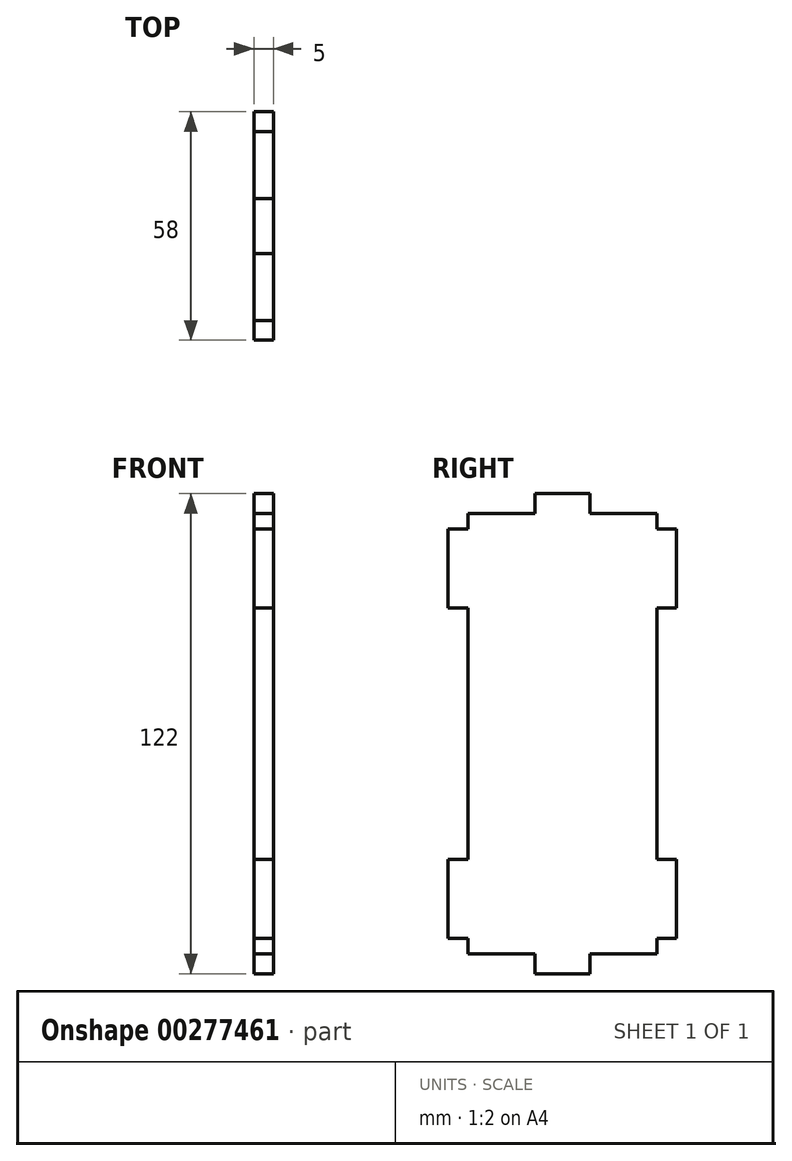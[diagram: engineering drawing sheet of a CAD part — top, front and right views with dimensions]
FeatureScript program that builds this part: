
annotation { "Feature Type Name" : "Feature", "Feature Type Description" : "" }
export const myFeature = defineFeature(function(context is Context, id is Id, definition is map)
    precondition{}
    {
        {
            var Q0;
            Q0=qCreatedBy(makeId("Right.planeOp"),FACE);
            var sketch = newSketch(context, id + "F0", { "sketchPlane" : qUnion([Q0])});
            skLineSegment(sketch, "E0.bottom", {"start": v(-24, 56) * mm, "end": v(-7, 56) * mm});
            skLineSegment(sketch, "E0.top", {"start": v(-24, -56) * mm, "end": v(-7, -56) * mm});
            skLineSegment(sketch, "E0.left", {"start": v(-24, 56) * mm, "end": v(-24, 52) * mm});
            skLineSegment(sketch, "E0.right", {"start": v(24, 56) * mm, "end": v(24, 52) * mm});
            skLineSegment(sketch, "E1.bottom", {"start": v(-24, 52) * mm, "end": v(-29, 52) * mm});
            skLineSegment(sketch, "E1.top", {"start": v(-24, 32) * mm, "end": v(-29, 32) * mm});
            skLineSegment(sketch, "E1.right", {"start": v(-29, 52) * mm, "end": v(-29, 32) * mm});
            skLineSegment(sketch, "E2.bottom", {"start": v(-24, -32) * mm, "end": v(-29, -32) * mm});
            skLineSegment(sketch, "E2.top", {"start": v(-24, -52) * mm, "end": v(-29, -52) * mm});
            skLineSegment(sketch, "E2.right", {"start": v(-29, -32) * mm, "end": v(-29, -52) * mm});
            skLineSegment(sketch, "E3.top", {"start": v(-7, 61) * mm, "end": v(7, 61) * mm});
            skLineSegment(sketch, "E3.left", {"start": v(-7, 56) * mm, "end": v(-7, 61) * mm});
            skLineSegment(sketch, "E3.right", {"start": v(7, 56) * mm, "end": v(7, 61) * mm});
            skLineSegment(sketch, "E4.top", {"start": v(-7, -61) * mm, "end": v(7, -61) * mm});
            skLineSegment(sketch, "E4.left", {"start": v(-7, -56) * mm, "end": v(-7, -61) * mm});
            skLineSegment(sketch, "E4.right", {"start": v(7, -56) * mm, "end": v(7, -61) * mm});
            skLineSegment(sketch, "E5.bottom", {"start": v(24, 52) * mm, "end": v(29, 52) * mm});
            skLineSegment(sketch, "E5.top", {"start": v(24, 32) * mm, "end": v(29, 32) * mm});
            skLineSegment(sketch, "E5.right", {"start": v(29, 52) * mm, "end": v(29, 32) * mm});
            skLineSegment(sketch, "E6.bottom", {"start": v(24, -32) * mm, "end": v(29, -32) * mm});
            skLineSegment(sketch, "E6.top", {"start": v(24, -52) * mm, "end": v(29, -52) * mm});
            skLineSegment(sketch, "E6.right", {"start": v(29, -32) * mm, "end": v(29, -52) * mm});
            skLineSegment(sketch, "E7.trimOffspring", {"start": v(7, 56) * mm, "end": v(24, 56) * mm});
            skLineSegment(sketch, "E8.trimOffspring", {"start": v(-24, -52) * mm, "end": v(-24, -56) * mm});
            skLineSegment(sketch, "E9.trimOffspring", {"start": v(24, 32) * mm, "end": v(24, -32) * mm});
            skLineSegment(sketch, "E10.trimOffspring", {"start": v(24, -52) * mm, "end": v(24, -56) * mm});
            skLineSegment(sketch, "E11.trimOffspring", {"start": v(7, -56) * mm, "end": v(24, -56) * mm});
            skLineSegment(sketch, "E12", {"start": v(-24, 32) * mm, "end": v(-24, -32) * mm});
            skSolve(sketch);
        }
        {
            var Q0;
            Q0=makeQuery(id+"F0.imprint","IMPRINT",FACE,{"disambiguationData":[TD([[makeQuery(id+"F0.imprint","IMPRINT",EDGE,{"derivedFrom":sQuery(id+"F0.wireOp",EDGE,"E0.bottom")}),-1.0]])]});
            extrude(context, id + "F1", {"entities" : qUnion([Q0]), "depth" : 5 * mm});
        }
    });
